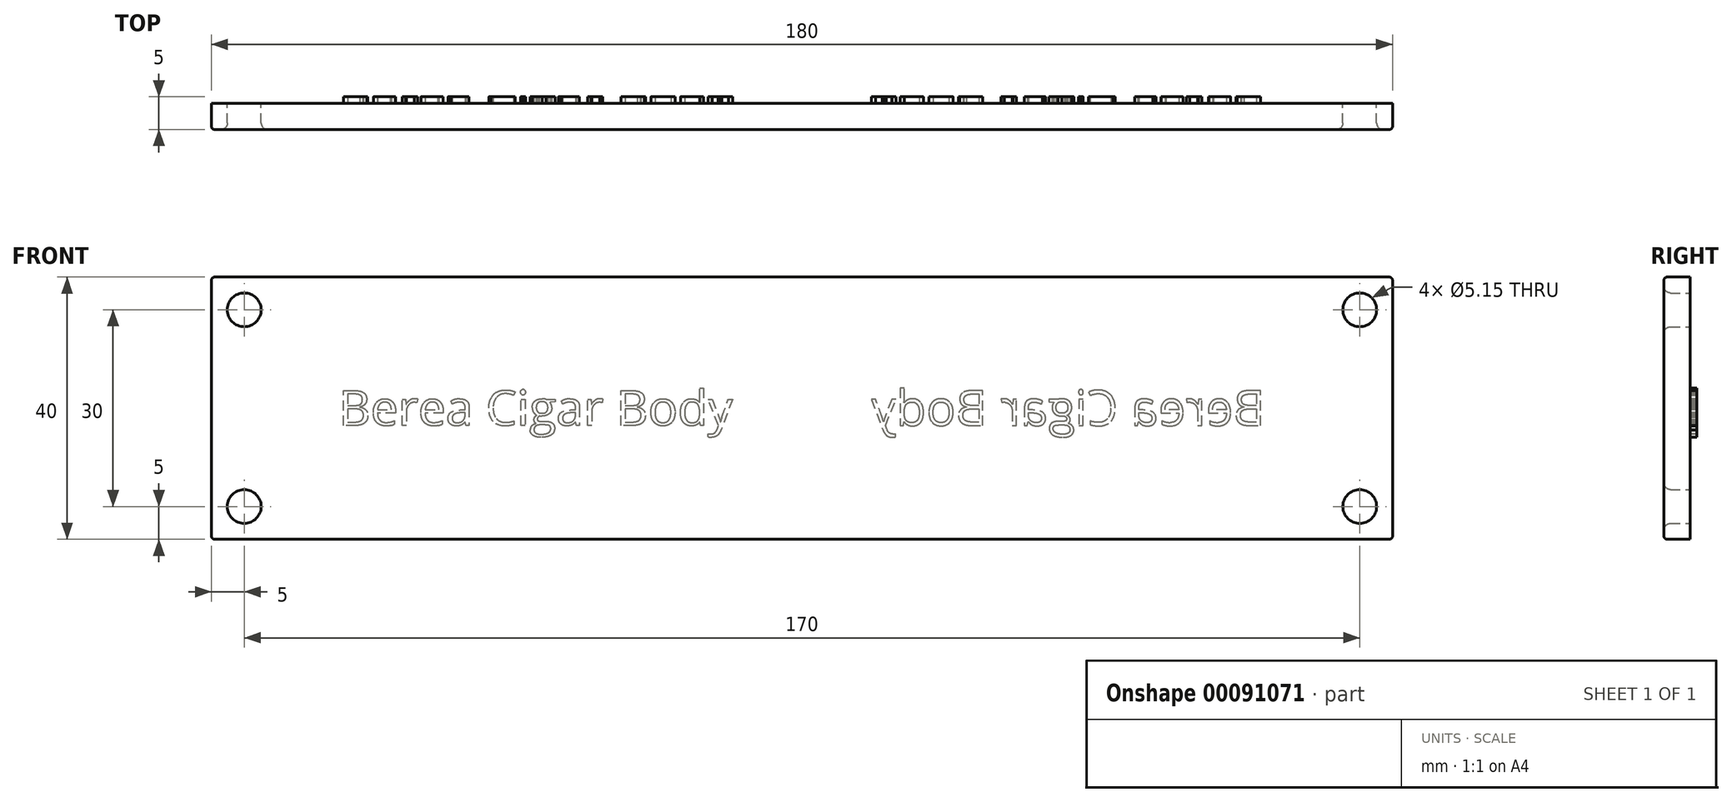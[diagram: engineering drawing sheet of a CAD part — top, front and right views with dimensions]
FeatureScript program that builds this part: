
annotation { "Feature Type Name" : "Feature", "Feature Type Description" : "" }
export const myFeature = defineFeature(function(context is Context, id is Id, definition is map)
    precondition{}
    {
        {
            var Q0;
            Q0=qCreatedBy(makeId("Front.planeOp"),FACE);
            var sketch = newSketch(context, id + "F0", { "sketchPlane" : qUnion([Q0])});
            skLineSegment(sketch, "E0.bottom", {"start": v(-90, -20) * mm, "end": v(90, -20) * mm});
            skLineSegment(sketch, "E0.top", {"start": v(-90, 20) * mm, "end": v(90, 20) * mm});
            skLineSegment(sketch, "E0.left", {"start": v(-90, -20) * mm, "end": v(-90, 20) * mm});
            skLineSegment(sketch, "E0.right", {"start": v(90, -20) * mm, "end": v(90, 20) * mm});
            skPoint(sketch, "E0.middle", {"position": v(0, 0) * mm});
            skCircle(sketch, "E1", {"center": v(-85, 15) * mm, "radius": 2.58 * mm});
            skPoint(sketch, "E2.start.orphan", {"position": v(-90, 0) * mm});
            skPoint(sketch, "E3.orphan", {"position": v(0, 20) * mm});
            skPoint(sketch, "E4.end.orphan", {"position": v(0, -20) * mm});
            skLineSegment(sketch, "E5", {"start": v(-90, 0) * mm, "end": v(0, 0) * mm, "construction": true});
            skLineSegment(sketch, "E6", {"start": v(0, 20) * mm, "end": v(0, -20) * mm, "construction": true});
            skCircle(sketch, "E7.MirrorC", {"center": v(-85, -15) * mm, "radius": 2.58 * mm});
            skCircle(sketch, "E8.MirrorC", {"center": v(85, 15) * mm, "radius": 2.58 * mm});
            skCircle(sketch, "E9.MirrorC", {"center": v(85, -15) * mm, "radius": 2.58 * mm});
            skSolve(sketch);
        }
        {
            var Q0;
            Q0=makeQuery(id+"F0.imprint","IMPRINT",FACE,{"disambiguationData":[TD([[makeQuery(id+"F0.imprint","IMPRINT",EDGE,{"derivedFrom":sQuery(id+"F0.wireOp",EDGE,"E0.bottom")}),1.0]])]});
            extrude(context, id + "F1", {"entities" : qUnion([Q0]), "depth" : 4 * mm});
        }
        {
            var Q0;
            Q0=makeQuery(id+"F1.opExtrude","CAP_EDGE",EDGE,{"disambiguationData":[OSD([sQuery(id+"F0.wireOp",EDGE,"E1")])],"isStart":false});
            var Q1;
            Q1=makeQuery(id+"F1.opExtrude","CAP_EDGE",EDGE,{"disambiguationData":[OSD([sQuery(id+"F0.wireOp",EDGE,"f5b72a5b-8583-449a-bdbf-9ac5a681e1fd0.MirrorC")])],"isStart":false});
            var Q2;
            Q2=makeQuery(id+"F1.opExtrude","CAP_EDGE",EDGE,{"disambiguationData":[OSD([sQuery(id+"F0.wireOp",EDGE,"2623e306-60f4-4522-aa65-1e3e8c2cf5b60.MirrorC")])],"isStart":false});
            var Q3;
            Q3=makeQuery(id+"F1.opExtrude","CAP_EDGE",EDGE,{"disambiguationData":[OSD([sQuery(id+"F0.wireOp",EDGE,"be81a34d-1d50-4ce7-a7a8-4484a1701fac0.MirrorC")])],"isStart":false});
            var Q4;
            Q4=makeQuery(id+"F1.opExtrude","CAP_EDGE",EDGE,{"disambiguationData":[OSD([sQuery(id+"F0.wireOp",EDGE,"E7.MirrorC")])],"isStart":false});
            var Q5;
            Q5=makeQuery(id+"F1.opExtrude","CAP_EDGE",EDGE,{"disambiguationData":[OSD([sQuery(id+"F0.wireOp",EDGE,"E8.MirrorC")])],"isStart":false});
            var Q6;
            Q6=makeQuery(id+"F1.opExtrude","CAP_EDGE",EDGE,{"disambiguationData":[OSD([sQuery(id+"F0.wireOp",EDGE,"E9.MirrorC")])],"isStart":false});
            fillet(context, id + "F2", {"entities" : qUnion([Q0, Q1, Q2, Q3, Q4, Q5, Q6]), "radius" : 1 * mm, "tangentPropagation" : true, "allowEdgeOverflow" : false});
        }
        {
            var Q0;
            Q0=makeQuery(id+"F1.opExtrude","CAP_EDGE",EDGE,{"disambiguationData":[OSD([sQuery(id+"F0.wireOp",EDGE,"E0.top")])],"isStart":false});
            var Q1;
            Q1=makeQuery(id+"F1.opExtrude","CAP_EDGE",EDGE,{"disambiguationData":[OSD([sQuery(id+"F0.wireOp",EDGE,"E0.left")])],"isStart":false});
            var Q2;
            Q2=makeQuery(id+"F1.opExtrude","CAP_EDGE",EDGE,{"disambiguationData":[OSD([sQuery(id+"F0.wireOp",EDGE,"E0.bottom")])],"isStart":false});
            var Q3;
            Q3=makeQuery(id+"F1.opExtrude","CAP_EDGE",EDGE,{"disambiguationData":[OSD([sQuery(id+"F0.wireOp",EDGE,"E0.right")])],"isStart":false});
            var Q4;
            Q4=makeQuery(id+"F1.opExtrude","SWEPT_EDGE",EDGE,{"disambiguationData":[OSD([sQuery(id+"F0.wireOp",EDGE,"E0.top"),sQuery(id+"F0.wireOp",EDGE,"E0.left")])]});
            var Q5;
            Q5=makeQuery(id+"F1.opExtrude","SWEPT_EDGE",EDGE,{"disambiguationData":[OSD([sQuery(id+"F0.wireOp",EDGE,"E0.bottom"),sQuery(id+"F0.wireOp",EDGE,"E0.left")])]});
            var Q6;
            Q6=makeQuery(id+"F1.opExtrude","SWEPT_EDGE",EDGE,{"disambiguationData":[OSD([sQuery(id+"F0.wireOp",EDGE,"E0.top"),sQuery(id+"F0.wireOp",EDGE,"E0.right")])]});
            var Q7;
            Q7=makeQuery(id+"F1.opExtrude","SWEPT_EDGE",EDGE,{"disambiguationData":[OSD([sQuery(id+"F0.wireOp",EDGE,"E0.bottom"),sQuery(id+"F0.wireOp",EDGE,"E0.right")])]});
            fillet(context, id + "F3", {"entities" : qUnion([Q0, Q1, Q2, Q3, Q4, Q5, Q6, Q7]), "radius" : .5 * mm, "tangentPropagation" : true, "allowEdgeOverflow" : false});
        }
        {
            var Q0;
            Q0=makeQuery(id+"F1.opExtrude","CAP_FACE",FACE,{"disambiguationData":[OSD([sQuery(id+"F0.wireOp",EDGE,"E0.bottom"),sQuery(id+"F0.wireOp",EDGE,"E0.top"),sQuery(id+"F0.wireOp",EDGE,"E0.left"),sQuery(id+"F0.wireOp",EDGE,"E0.right"),sQuery(id+"F0.wireOp",EDGE,"E1"),sQuery(id+"F0.wireOp",EDGE,"E7.MirrorC"),sQuery(id+"F0.wireOp",EDGE,"E8.MirrorC"),sQuery(id+"F0.wireOp",EDGE,"E9.MirrorC")])],"isStart":true});
            var sketch = newSketch(context, id + "F4", { "sketchPlane" : qUnion([Q0])});
            skText(sketch, "E10", { "text": "Berea Cigar Body", "fontName": "OpenSans-Regular.ttf"});
            skLineSegment(sketch, "E11", {"start": v(0, 20) * mm, "end": v(0, -20) * mm, "construction": true});
            const initialGuessF4  = {"E10": [-0.0706, -0.00264, 1, 0, 0.00539]};
            skSetInitialGuess(sketch, initialGuessF4);
            skSolve(sketch);
        }
        {
            var Q0;
            Q0=qSketchRegion(id+"F4",true);
            extrude(context, id + "F5", {"entities" : qUnion([Q0]), "operationType" : NewBodyOperationType.ADD, "depth" : 1 * mm});
        }
        {
            var Q0;
            Q0=makeQuery(id+"F1.opExtrude","SWEPT_BODY",BODY,{"disambiguationData":[OSD([sQuery(id+"F0.wireOp",EDGE,"E0.bottom"),sQuery(id+"F0.wireOp",EDGE,"E0.top"),sQuery(id+"F0.wireOp",EDGE,"E0.left"),sQuery(id+"F0.wireOp",EDGE,"E0.right"),sQuery(id+"F0.wireOp",EDGE,"E1"),sQuery(id+"F0.wireOp",EDGE,"E7.MirrorC"),sQuery(id+"F0.wireOp",EDGE,"E8.MirrorC"),sQuery(id+"F0.wireOp",EDGE,"E9.MirrorC")])]});
            var Q1;
            Q1=makeQuery(id+"F5.opExtrude","SWEPT_FACE",FACE,{"disambiguationData":[OSD([sQuery(id+"F4.wireOp",EDGE,"E10.sketch_text.stroke-94")])]});
            var Q2;
            Q2=makeQuery(id+"F5.opExtrude","SWEPT_FACE",FACE,{"disambiguationData":[OSD([sQuery(id+"F4.wireOp",EDGE,"E10.sketch_text.stroke-169")])]});
            var Q3;
            Q3=makeQuery(id+"F5.opExtrude","SWEPT_FACE",FACE,{"disambiguationData":[OSD([sQuery(id+"F4.wireOp",EDGE,"E10.sketch_text.stroke-185")])]});
            var Q4;
            Q4=makeQuery(id+"F5.opExtrude","SWEPT_FACE",FACE,{"disambiguationData":[OSD([sQuery(id+"F4.wireOp",EDGE,"E10.sketch_text.stroke-125")])]});
            var Q5;
            Q5=makeQuery(id+"F5.opExtrude","SWEPT_FACE",FACE,{"disambiguationData":[OSD([sQuery(id+"F4.wireOp",EDGE,"E10.sketch_text.stroke-155")])]});
            var Q6;
            Q6=makeQuery(id+"F5.opExtrude","SWEPT_FACE",FACE,{"disambiguationData":[OSD([sQuery(id+"F4.wireOp",EDGE,"E10.sketch_text.stroke-65")])]});
            var Q7;
            Q7=makeQuery(id+"F5.opExtrude","SWEPT_FACE",FACE,{"disambiguationData":[OSD([sQuery(id+"F4.wireOp",EDGE,"E10.sketch_text.stroke-81")])]});
            var Q8;
            Q8=makeQuery(id+"F5.opExtrude","SWEPT_FACE",FACE,{"disambiguationData":[OSD([sQuery(id+"F4.wireOp",EDGE,"E10.sketch_text.stroke-67")])]});
            var Q9;
            Q9=makeQuery(id+"F5.opExtrude","SWEPT_FACE",FACE,{"disambiguationData":[OSD([sQuery(id+"F4.wireOp",EDGE,"E10.sketch_text.stroke-99")])]});
            var Q10;
            Q10=makeQuery(id+"F5.opExtrude","SWEPT_FACE",FACE,{"disambiguationData":[OSD([sQuery(id+"F4.wireOp",EDGE,"E10.sketch_text.stroke-127")])]});
            var Q11;
            Q11=makeQuery(id+"F5.opExtrude","SWEPT_FACE",FACE,{"disambiguationData":[OSD([sQuery(id+"F4.wireOp",EDGE,"E10.sketch_text.stroke-10")])]});
            var Q12;
            Q12=makeQuery(id+"F5.opExtrude","CAP_FACE",FACE,{"disambiguationData":[OSD([sQuery(id+"F4.wireOp",EDGE,"E10.sketch_text.stroke-9"),sQuery(id+"F4.wireOp",EDGE,"E10.sketch_text.stroke-10"),sQuery(id+"F4.wireOp",EDGE,"E10.sketch_text.stroke-11"),sQuery(id+"F4.wireOp",EDGE,"E10.sketch_text.stroke-12")])],"isStart":false});
            var Q13;
            Q13=makeQuery(id+"F5.opExtrude","SWEPT_FACE",FACE,{"disambiguationData":[OSD([sQuery(id+"F4.wireOp",EDGE,"E10.sketch_text.stroke-154")])]});
            var Q14;
            Q14=makeQuery(id+"F5.opExtrude","SWEPT_FACE",FACE,{"disambiguationData":[OSD([sQuery(id+"F4.wireOp",EDGE,"E10.sketch_text.stroke-1")])]});
            var Q15;
            Q15=makeQuery(id+"F5.opExtrude","CAP_FACE",FACE,{"disambiguationData":[OSD([sQuery(id+"F4.wireOp",EDGE,"E10.sketch_text.stroke-124"),sQuery(id+"F4.wireOp",EDGE,"E10.sketch_text.stroke-125"),sQuery(id+"F4.wireOp",EDGE,"E10.sketch_text.stroke-126"),sQuery(id+"F4.wireOp",EDGE,"E10.sketch_text.stroke-127"),sQuery(id+"F4.wireOp",EDGE,"E10.sketch_text.stroke-128"),sQuery(id+"F4.wireOp",EDGE,"E10.sketch_text.stroke-129"),sQuery(id+"F4.wireOp",EDGE,"E10.sketch_text.stroke-130"),sQuery(id+"F4.wireOp",EDGE,"E10.sketch_text.stroke-131"),sQuery(id+"F4.wireOp",EDGE,"E10.sketch_text.stroke-132"),sQuery(id+"F4.wireOp",EDGE,"E10.sketch_text.stroke-133"),sQuery(id+"F4.wireOp",EDGE,"E10.sketch_text.stroke-134"),sQuery(id+"F4.wireOp",EDGE,"E10.sketch_text.stroke-135"),sQuery(id+"F4.wireOp",EDGE,"E10.sketch_text.stroke-136"),sQuery(id+"F4.wireOp",EDGE,"E10.sketch_text.stroke-137"),sQuery(id+"F4.wireOp",EDGE,"E10.sketch_text.stroke-138")])],"isStart":false});
            var Q16;
            Q16=makeQuery(id+"F5.opExtrude","CAP_FACE",FACE,{"disambiguationData":[OSD([sQuery(id+"F4.wireOp",EDGE,"E10.sketch_text.stroke-34"),sQuery(id+"F4.wireOp",EDGE,"E10.sketch_text.stroke-35"),sQuery(id+"F4.wireOp",EDGE,"E10.sketch_text.stroke-36"),sQuery(id+"F4.wireOp",EDGE,"E10.sketch_text.stroke-37"),sQuery(id+"F4.wireOp",EDGE,"E10.sketch_text.stroke-38"),sQuery(id+"F4.wireOp",EDGE,"E10.sketch_text.stroke-39"),sQuery(id+"F4.wireOp",EDGE,"E10.sketch_text.stroke-40"),sQuery(id+"F4.wireOp",EDGE,"E10.sketch_text.stroke-41"),sQuery(id+"F4.wireOp",EDGE,"E10.sketch_text.stroke-42"),sQuery(id+"F4.wireOp",EDGE,"E10.sketch_text.stroke-43"),sQuery(id+"F4.wireOp",EDGE,"E10.sketch_text.stroke-44"),sQuery(id+"F4.wireOp",EDGE,"E10.sketch_text.stroke-45"),sQuery(id+"F4.wireOp",EDGE,"E10.sketch_text.stroke-46"),sQuery(id+"F4.wireOp",EDGE,"E10.sketch_text.stroke-47"),sQuery(id+"F4.wireOp",EDGE,"E10.sketch_text.stroke-48"),sQuery(id+"F4.wireOp",EDGE,"E10.sketch_text.stroke-49"),sQuery(id+"F4.wireOp",EDGE,"E10.sketch_text.stroke-50"),sQuery(id+"F4.wireOp",EDGE,"E10.sketch_text.stroke-51"),sQuery(id+"F4.wireOp",EDGE,"E10.sketch_text.stroke-52"),sQuery(id+"F4.wireOp",EDGE,"E10.sketch_text.stroke-53"),sQuery(id+"F4.wireOp",EDGE,"E10.sketch_text.stroke-54"),sQuery(id+"F4.wireOp",EDGE,"E10.sketch_text.stroke-55"),sQuery(id+"F4.wireOp",EDGE,"E10.sketch_text.stroke-56"),sQuery(id+"F4.wireOp",EDGE,"E10.sketch_text.stroke-57"),sQuery(id+"F4.wireOp",EDGE,"E10.sketch_text.stroke-58"),sQuery(id+"F4.wireOp",EDGE,"E10.sketch_text.stroke-59"),sQuery(id+"F4.wireOp",EDGE,"E10.sketch_text.stroke-60")])],"isStart":false});
            var Q17;
            Q17=makeQuery(id+"F5.opExtrude","SWEPT_FACE",FACE,{"disambiguationData":[OSD([sQuery(id+"F4.wireOp",EDGE,"E10.sketch_text.stroke-50")])]});
            var Q18;
            Q18=makeQuery(id+"F5.opExtrude","SWEPT_FACE",FACE,{"disambiguationData":[OSD([sQuery(id+"F4.wireOp",EDGE,"E10.sketch_text.stroke-2")])]});
            var Q19;
            Q19=makeQuery(id+"F5.opExtrude","SWEPT_FACE",FACE,{"disambiguationData":[OSD([sQuery(id+"F4.wireOp",EDGE,"E10.sketch_text.stroke-3")])]});
            var Q20;
            Q20=makeQuery(id+"F5.opExtrude","SWEPT_FACE",FACE,{"disambiguationData":[OSD([sQuery(id+"F4.wireOp",EDGE,"E10.sketch_text.stroke-5")])]});
            var Q21;
            Q21=makeQuery(id+"F5.opExtrude","SWEPT_FACE",FACE,{"disambiguationData":[OSD([sQuery(id+"F4.wireOp",EDGE,"E10.sketch_text.stroke-8")])]});
            var Q22;
            Q22=makeQuery(id+"F5.opExtrude","SWEPT_FACE",FACE,{"disambiguationData":[OSD([sQuery(id+"F4.wireOp",EDGE,"E10.sketch_text.stroke-98")])]});
            var Q23;
            Q23=makeQuery(id+"F5.opExtrude","SWEPT_FACE",FACE,{"disambiguationData":[OSD([sQuery(id+"F4.wireOp",EDGE,"E10.sketch_text.stroke-66")])]});
            var Q24;
            Q24=makeQuery(id+"F5.opExtrude","SWEPT_FACE",FACE,{"disambiguationData":[OSD([sQuery(id+"F4.wireOp",EDGE,"E10.sketch_text.stroke-153")])]});
            var Q25;
            Q25=makeQuery(id+"F5.opExtrude","SWEPT_FACE",FACE,{"disambiguationData":[OSD([sQuery(id+"F4.wireOp",EDGE,"E10.sketch_text.stroke-126")])]});
            var Q26;
            Q26=makeQuery(id+"F5.opExtrude","SWEPT_FACE",FACE,{"disambiguationData":[OSD([sQuery(id+"F4.wireOp",EDGE,"E10.sketch_text.stroke-183")])]});
            var Q27;
            Q27=makeQuery(id+"F5.opExtrude","SWEPT_FACE",FACE,{"disambiguationData":[OSD([sQuery(id+"F4.wireOp",EDGE,"E10.sketch_text.stroke-109")])]});
            var Q28;
            Q28=makeQuery(id+"F5.opExtrude","SWEPT_FACE",FACE,{"disambiguationData":[OSD([sQuery(id+"F4.wireOp",EDGE,"E10.sketch_text.stroke-186")])]});
            var Q29;
            Q29=makeQuery(id+"F5.opExtrude","SWEPT_FACE",FACE,{"disambiguationData":[OSD([sQuery(id+"F4.wireOp",EDGE,"E10.sketch_text.stroke-79")])]});
            var Q30;
            Q30=makeQuery(id+"F5.opExtrude","SWEPT_FACE",FACE,{"disambiguationData":[OSD([sQuery(id+"F4.wireOp",EDGE,"E10.sketch_text.stroke-110")])]});
            var Q31;
            Q31=makeQuery(id+"F5.opExtrude","SWEPT_FACE",FACE,{"disambiguationData":[OSD([sQuery(id+"F4.wireOp",EDGE,"E10.sketch_text.stroke-38")])]});
            var Q32;
            Q32=makeQuery(id+"F5.opExtrude","SWEPT_FACE",FACE,{"disambiguationData":[OSD([sQuery(id+"F4.wireOp",EDGE,"E10.sketch_text.stroke-24")])]});
            var Q33;
            Q33=makeQuery(id+"F5.opExtrude","SWEPT_FACE",FACE,{"disambiguationData":[OSD([sQuery(id+"F4.wireOp",EDGE,"E10.sketch_text.stroke-12")])]});
            var Q34;
            Q34=makeQuery(id+"F5.opExtrude","SWEPT_FACE",FACE,{"disambiguationData":[OSD([sQuery(id+"F4.wireOp",EDGE,"E10.sketch_text.stroke-100")])]});
            var Q35;
            Q35=makeQuery(id+"F5.opExtrude","SWEPT_FACE",FACE,{"disambiguationData":[OSD([sQuery(id+"F4.wireOp",EDGE,"E10.sketch_text.stroke-158")])]});
            var Q36;
            Q36=makeQuery(id+"F5.opExtrude","SWEPT_FACE",FACE,{"disambiguationData":[OSD([sQuery(id+"F4.wireOp",EDGE,"E10.sketch_text.stroke-142")])]});
            var Q37;
            Q37=makeQuery(id+"F5.opExtrude","SWEPT_FACE",FACE,{"disambiguationData":[OSD([sQuery(id+"F4.wireOp",EDGE,"E10.sketch_text.stroke-54")])]});
            var Q38;
            Q38=makeQuery(id+"F5.opExtrude","SWEPT_FACE",FACE,{"disambiguationData":[OSD([sQuery(id+"F4.wireOp",EDGE,"E10.sketch_text.stroke-25")])]});
            var Q39;
            Q39=makeQuery(id+"F5.opExtrude","SWEPT_FACE",FACE,{"disambiguationData":[OSD([sQuery(id+"F4.wireOp",EDGE,"E10.sketch_text.stroke-101")])]});
            var Q40;
            Q40=makeQuery(id+"F5.opExtrude","SWEPT_FACE",FACE,{"disambiguationData":[OSD([sQuery(id+"F4.wireOp",EDGE,"E10.sketch_text.stroke-69")])]});
            var Q41;
            Q41=makeQuery(id+"F5.opExtrude","SWEPT_FACE",FACE,{"disambiguationData":[OSD([sQuery(id+"F4.wireOp",EDGE,"E10.sketch_text.stroke-159")])]});
            var Q42;
            Q42=makeQuery(id+"F5.opExtrude","SWEPT_FACE",FACE,{"disambiguationData":[OSD([sQuery(id+"F4.wireOp",EDGE,"E10.sketch_text.stroke-85")])]});
            var Q43;
            Q43=makeQuery(id+"F5.opExtrude","SWEPT_FACE",FACE,{"disambiguationData":[OSD([sQuery(id+"F4.wireOp",EDGE,"E10.sketch_text.stroke-173")])]});
            var Q44;
            Q44=makeQuery(id+"F5.opExtrude","SWEPT_FACE",FACE,{"disambiguationData":[OSD([sQuery(id+"F4.wireOp",EDGE,"E10.sketch_text.stroke-40")])]});
            var Q45;
            Q45=makeQuery(id+"F5.opExtrude","SWEPT_FACE",FACE,{"disambiguationData":[OSD([sQuery(id+"F4.wireOp",EDGE,"E10.sketch_text.stroke-102")])]});
            var Q46;
            Q46=makeQuery(id+"F5.opExtrude","SWEPT_FACE",FACE,{"disambiguationData":[OSD([sQuery(id+"F4.wireOp",EDGE,"E10.sketch_text.stroke-86")])]});
            var Q47;
            Q47=makeQuery(id+"F5.opExtrude","SWEPT_FACE",FACE,{"disambiguationData":[OSD([sQuery(id+"F4.wireOp",EDGE,"E10.sketch_text.stroke-130")])]});
            var Q48;
            Q48=makeQuery(id+"F5.opExtrude","SWEPT_FACE",FACE,{"disambiguationData":[OSD([sQuery(id+"F4.wireOp",EDGE,"E10.sketch_text.stroke-103")])]});
            var Q49;
            Q49=makeQuery(id+"F5.opExtrude","SWEPT_FACE",FACE,{"disambiguationData":[OSD([sQuery(id+"F4.wireOp",EDGE,"E10.sketch_text.stroke-87")])]});
            var Q50;
            Q50=makeQuery(id+"F5.opExtrude","SWEPT_FACE",FACE,{"disambiguationData":[OSD([sQuery(id+"F4.wireOp",EDGE,"E10.sketch_text.stroke-145")])]});
            var Q51;
            Q51=makeQuery(id+"F5.opExtrude","SWEPT_FACE",FACE,{"disambiguationData":[OSD([sQuery(id+"F4.wireOp",EDGE,"E10.sketch_text.stroke-131")])]});
            var Q52;
            Q52=makeQuery(id+"F5.opExtrude","SWEPT_FACE",FACE,{"disambiguationData":[OSD([sQuery(id+"F4.wireOp",EDGE,"E10.sketch_text.stroke-28")])]});
            var Q53;
            Q53=makeQuery(id+"F5.opExtrude","SWEPT_FACE",FACE,{"disambiguationData":[OSD([sQuery(id+"F4.wireOp",EDGE,"E10.sketch_text.stroke-14")])]});
            var Q54;
            Q54=makeQuery(id+"F5.opExtrude","SWEPT_FACE",FACE,{"disambiguationData":[OSD([sQuery(id+"F4.wireOp",EDGE,"E10.sketch_text.stroke-88")])]});
            var Q55;
            Q55=makeQuery(id+"F5.opExtrude","SWEPT_FACE",FACE,{"disambiguationData":[OSD([sQuery(id+"F4.wireOp",EDGE,"E10.sketch_text.stroke-162")])]});
            var Q56;
            Q56=makeQuery(id+"F5.opExtrude","SWEPT_FACE",FACE,{"disambiguationData":[OSD([sQuery(id+"F4.wireOp",EDGE,"E10.sketch_text.stroke-176")])]});
            var Q57;
            Q57=makeQuery(id+"F5.opExtrude","SWEPT_FACE",FACE,{"disambiguationData":[OSD([sQuery(id+"F4.wireOp",EDGE,"E10.sketch_text.stroke-73")])]});
            var Q58;
            Q58=makeQuery(id+"F5.opExtrude","SWEPT_FACE",FACE,{"disambiguationData":[OSD([sQuery(id+"F4.wireOp",EDGE,"E10.sketch_text.stroke-59")])]});
            var Q59;
            Q59=makeQuery(id+"F5.opExtrude","SWEPT_FACE",FACE,{"disambiguationData":[OSD([sQuery(id+"F4.wireOp",EDGE,"E10.sketch_text.stroke-133")])]});
            var Q60;
            Q60=makeQuery(id+"F5.opExtrude","SWEPT_FACE",FACE,{"disambiguationData":[OSD([sQuery(id+"F4.wireOp",EDGE,"E10.sketch_text.stroke-119")])]});
            var Q61;
            Q61=makeQuery(id+"F5.opExtrude","SWEPT_FACE",FACE,{"disambiguationData":[OSD([sQuery(id+"F4.wireOp",EDGE,"E10.sketch_text.stroke-74")])]});
            var Q62;
            Q62=makeQuery(id+"F5.opExtrude","SWEPT_FACE",FACE,{"disambiguationData":[OSD([sQuery(id+"F4.wireOp",EDGE,"E10.sketch_text.stroke-44")])]});
            var Q63;
            Q63=makeQuery(id+"F5.opExtrude","SWEPT_FACE",FACE,{"disambiguationData":[OSD([sQuery(id+"F4.wireOp",EDGE,"E10.sketch_text.stroke-120")])]});
            var Q64;
            Q64=makeQuery(id+"F5.opExtrude","SWEPT_FACE",FACE,{"disambiguationData":[OSD([sQuery(id+"F4.wireOp",EDGE,"E10.sketch_text.stroke-90")])]});
            var Q65;
            Q65=makeQuery(id+"F5.opExtrude","SWEPT_FACE",FACE,{"disambiguationData":[OSD([sQuery(id+"F4.wireOp",EDGE,"E10.sketch_text.stroke-178")])]});
            var Q66;
            Q66=makeQuery(id+"F5.opExtrude","SWEPT_FACE",FACE,{"disambiguationData":[OSD([sQuery(id+"F4.wireOp",EDGE,"E10.sketch_text.stroke-45")])]});
            var Q67;
            Q67=makeQuery(id+"F5.opExtrude","SWEPT_FACE",FACE,{"disambiguationData":[OSD([sQuery(id+"F4.wireOp",EDGE,"E10.sketch_text.stroke-31")])]});
            var Q68;
            Q68=makeQuery(id+"F5.opExtrude","SWEPT_FACE",FACE,{"disambiguationData":[OSD([sQuery(id+"F4.wireOp",EDGE,"E10.sketch_text.stroke-135")])]});
            var Q69;
            Q69=makeQuery(id+"F5.opExtrude","SWEPT_FACE",FACE,{"disambiguationData":[OSD([sQuery(id+"F4.wireOp",EDGE,"E10.sketch_text.stroke-179")])]});
            var Q70;
            Q70=makeQuery(id+"F5.opExtrude","SWEPT_FACE",FACE,{"disambiguationData":[OSD([sQuery(id+"F4.wireOp",EDGE,"E10.sketch_text.stroke-165")])]});
            var Q71;
            Q71=makeQuery(id+"F5.opExtrude","SWEPT_FACE",FACE,{"disambiguationData":[OSD([sQuery(id+"F4.wireOp",EDGE,"E10.sketch_text.stroke-149")])]});
            var Q72;
            Q72=makeQuery(id+"F5.opExtrude","SWEPT_FACE",FACE,{"disambiguationData":[OSD([sQuery(id+"F4.wireOp",EDGE,"E10.sketch_text.stroke-136")])]});
            var Q73;
            Q73=makeQuery(id+"F5.opExtrude","SWEPT_FACE",FACE,{"disambiguationData":[OSD([sQuery(id+"F4.wireOp",EDGE,"E10.sketch_text.stroke-122")])]});
            var Q74;
            Q74=makeQuery(id+"F5.opExtrude","SWEPT_FACE",FACE,{"disambiguationData":[OSD([sQuery(id+"F4.wireOp",EDGE,"E10.sketch_text.stroke-106")])]});
            var Q75;
            Q75=makeQuery(id+"F5.opExtrude","SWEPT_FACE",FACE,{"disambiguationData":[OSD([sQuery(id+"F4.wireOp",EDGE,"E10.sketch_text.stroke-180")])]});
            var Q76;
            Q76=makeQuery(id+"F5.opExtrude","SWEPT_FACE",FACE,{"disambiguationData":[OSD([sQuery(id+"F4.wireOp",EDGE,"E10.sketch_text.stroke-166")])]});
            var Q77;
            Q77=makeQuery(id+"F5.opExtrude","SWEPT_FACE",FACE,{"disambiguationData":[OSD([sQuery(id+"F4.wireOp",EDGE,"E10.sketch_text.stroke-150")])]});
            var Q78;
            Q78=makeQuery(id+"F5.opExtrude","SWEPT_FACE",FACE,{"disambiguationData":[OSD([sQuery(id+"F4.wireOp",EDGE,"E10.sketch_text.stroke-76")])]});
            var Q79;
            Q79=makeQuery(id+"F5.opExtrude","SWEPT_FACE",FACE,{"disambiguationData":[OSD([sQuery(id+"F4.wireOp",EDGE,"E10.sketch_text.stroke-32")])]});
            var Q80;
            Q80=makeQuery(id+"F5.opExtrude","SWEPT_FACE",FACE,{"disambiguationData":[OSD([sQuery(id+"F4.wireOp",EDGE,"E10.sketch_text.stroke-181")])]});
            var Q81;
            Q81=makeQuery(id+"F5.opExtrude","SWEPT_FACE",FACE,{"disambiguationData":[OSD([sQuery(id+"F4.wireOp",EDGE,"E10.sketch_text.stroke-47")])]});
            var Q82;
            Q82=makeQuery(id+"F5.opExtrude","SWEPT_FACE",FACE,{"disambiguationData":[OSD([sQuery(id+"F4.wireOp",EDGE,"E10.sketch_text.stroke-123")])]});
            var Q83;
            Q83=makeQuery(id+"F5.opExtrude","SWEPT_FACE",FACE,{"disambiguationData":[OSD([sQuery(id+"F4.wireOp",EDGE,"E10.sketch_text.stroke-107")])]});
            var Q84;
            Q84=makeQuery(id+"F5.opExtrude","SWEPT_FACE",FACE,{"disambiguationData":[OSD([sQuery(id+"F4.wireOp",EDGE,"E10.sketch_text.stroke-48")])]});
            var Q85;
            Q85=makeQuery(id+"F5.opExtrude","SWEPT_FACE",FACE,{"disambiguationData":[OSD([sQuery(id+"F4.wireOp",EDGE,"E10.sketch_text.stroke-124")])]});
            var Q86;
            Q86=makeQuery(id+"F5.opExtrude","SWEPT_FACE",FACE,{"disambiguationData":[OSD([sQuery(id+"F4.wireOp",EDGE,"E10.sketch_text.stroke-108")])]});
            var Q87;
            Q87=makeQuery(id+"F5.opExtrude","CAP_FACE",FACE,{"disambiguationData":[OSD([sQuery(id+"F4.wireOp",EDGE,"E10.sketch_text.stroke-139"),sQuery(id+"F4.wireOp",EDGE,"E10.sketch_text.stroke-140"),sQuery(id+"F4.wireOp",EDGE,"E10.sketch_text.stroke-141"),sQuery(id+"F4.wireOp",EDGE,"E10.sketch_text.stroke-142"),sQuery(id+"F4.wireOp",EDGE,"E10.sketch_text.stroke-143"),sQuery(id+"F4.wireOp",EDGE,"E10.sketch_text.stroke-144"),sQuery(id+"F4.wireOp",EDGE,"E10.sketch_text.stroke-145"),sQuery(id+"F4.wireOp",EDGE,"E10.sketch_text.stroke-146"),sQuery(id+"F4.wireOp",EDGE,"E10.sketch_text.stroke-147"),sQuery(id+"F4.wireOp",EDGE,"E10.sketch_text.stroke-148"),sQuery(id+"F4.wireOp",EDGE,"E10.sketch_text.stroke-149"),sQuery(id+"F4.wireOp",EDGE,"E10.sketch_text.stroke-150"),sQuery(id+"F4.wireOp",EDGE,"E10.sketch_text.stroke-151"),sQuery(id+"F4.wireOp",EDGE,"E10.sketch_text.stroke-152"),sQuery(id+"F4.wireOp",EDGE,"E10.sketch_text.stroke-153"),sQuery(id+"F4.wireOp",EDGE,"E10.sketch_text.stroke-154"),sQuery(id+"F4.wireOp",EDGE,"E10.sketch_text.stroke-155"),sQuery(id+"F4.wireOp",EDGE,"E10.sketch_text.stroke-156"),sQuery(id+"F4.wireOp",EDGE,"E10.sketch_text.stroke-157"),sQuery(id+"F4.wireOp",EDGE,"E10.sketch_text.stroke-158"),sQuery(id+"F4.wireOp",EDGE,"E10.sketch_text.stroke-159"),sQuery(id+"F4.wireOp",EDGE,"E10.sketch_text.stroke-160"),sQuery(id+"F4.wireOp",EDGE,"E10.sketch_text.stroke-161"),sQuery(id+"F4.wireOp",EDGE,"E10.sketch_text.stroke-162"),sQuery(id+"F4.wireOp",EDGE,"E10.sketch_text.stroke-163"),sQuery(id+"F4.wireOp",EDGE,"E10.sketch_text.stroke-164"),sQuery(id+"F4.wireOp",EDGE,"E10.sketch_text.stroke-165")])],"isStart":false});
            var Q88;
            Q88=makeQuery(id+"F5.opExtrude","CAP_FACE",FACE,{"disambiguationData":[OSD([sQuery(id+"F4.wireOp",EDGE,"E10.sketch_text.stroke-21"),sQuery(id+"F4.wireOp",EDGE,"E10.sketch_text.stroke-22"),sQuery(id+"F4.wireOp",EDGE,"E10.sketch_text.stroke-23"),sQuery(id+"F4.wireOp",EDGE,"E10.sketch_text.stroke-24"),sQuery(id+"F4.wireOp",EDGE,"E10.sketch_text.stroke-25"),sQuery(id+"F4.wireOp",EDGE,"E10.sketch_text.stroke-26"),sQuery(id+"F4.wireOp",EDGE,"E10.sketch_text.stroke-27"),sQuery(id+"F4.wireOp",EDGE,"E10.sketch_text.stroke-28"),sQuery(id+"F4.wireOp",EDGE,"E10.sketch_text.stroke-29"),sQuery(id+"F4.wireOp",EDGE,"E10.sketch_text.stroke-30"),sQuery(id+"F4.wireOp",EDGE,"E10.sketch_text.stroke-31"),sQuery(id+"F4.wireOp",EDGE,"E10.sketch_text.stroke-32"),sQuery(id+"F4.wireOp",EDGE,"E10.sketch_text.stroke-33")])],"isStart":false});
            var Q89;
            Q89=makeQuery(id+"F5.opExtrude","SWEPT_FACE",FACE,{"disambiguationData":[OSD([sQuery(id+"F4.wireOp",EDGE,"E10.sketch_text.stroke-113")])]});
            var Q90;
            Q90=makeQuery(id+"F5.opExtrude","SWEPT_FACE",FACE,{"disambiguationData":[OSD([sQuery(id+"F4.wireOp",EDGE,"E10.sketch_text.stroke-37")])]});
            var Q91;
            Q91=makeQuery(id+"F5.opExtrude","SWEPT_FACE",FACE,{"disambiguationData":[OSD([sQuery(id+"F4.wireOp",EDGE,"E10.sketch_text.stroke-187")])]});
            var Q92;
            Q92=makeQuery(id+"F5.opExtrude","SWEPT_FACE",FACE,{"disambiguationData":[OSD([sQuery(id+"F4.wireOp",EDGE,"E10.sketch_text.stroke-0")])]});
            var Q93;
            Q93=makeQuery(id+"F5.opExtrude","SWEPT_FACE",FACE,{"disambiguationData":[OSD([sQuery(id+"F4.wireOp",EDGE,"E10.sketch_text.stroke-4")])]});
            var Q94;
            Q94=makeQuery(id+"F5.opExtrude","SWEPT_FACE",FACE,{"disambiguationData":[OSD([sQuery(id+"F4.wireOp",EDGE,"E10.sketch_text.stroke-82")])]});
            var Q95;
            Q95=makeQuery(id+"F5.opExtrude","SWEPT_FACE",FACE,{"disambiguationData":[OSD([sQuery(id+"F4.wireOp",EDGE,"E10.sketch_text.stroke-52")])]});
            var Q96;
            Q96=makeQuery(id+"F5.opExtrude","SWEPT_FACE",FACE,{"disambiguationData":[OSD([sQuery(id+"F4.wireOp",EDGE,"E10.sketch_text.stroke-49")])]});
            var Q97;
            Q97=makeQuery(id+"F5.opExtrude","SWEPT_FACE",FACE,{"disambiguationData":[OSD([sQuery(id+"F4.wireOp",EDGE,"E10.sketch_text.stroke-63")])]});
            var Q98;
            Q98=makeQuery(id+"F5.opExtrude","SWEPT_FACE",FACE,{"disambiguationData":[OSD([sQuery(id+"F4.wireOp",EDGE,"E10.sketch_text.stroke-21")])]});
            var Q99;
            Q99=makeQuery(id+"F5.opExtrude","SWEPT_FACE",FACE,{"disambiguationData":[OSD([sQuery(id+"F4.wireOp",EDGE,"E10.sketch_text.stroke-128")])]});
            var Q100;
            Q100=makeQuery(id+"F5.opExtrude","SWEPT_FACE",FACE,{"disambiguationData":[OSD([sQuery(id+"F4.wireOp",EDGE,"E10.sketch_text.stroke-55")])]});
            var Q101;
            Q101=makeQuery(id+"F5.opExtrude","SWEPT_FACE",FACE,{"disambiguationData":[OSD([sQuery(id+"F4.wireOp",EDGE,"E10.sketch_text.stroke-26")])]});
            var Q102;
            Q102=makeQuery(id+"F5.opExtrude","SWEPT_FACE",FACE,{"disambiguationData":[OSD([sQuery(id+"F4.wireOp",EDGE,"E10.sketch_text.stroke-174")])]});
            var Q103;
            Q103=makeQuery(id+"F5.opExtrude","SWEPT_FACE",FACE,{"disambiguationData":[OSD([sQuery(id+"F4.wireOp",EDGE,"E10.sketch_text.stroke-104")])]});
            var Q104;
            Q104=makeQuery(id+"F5.opExtrude","SWEPT_FACE",FACE,{"disambiguationData":[OSD([sQuery(id+"F4.wireOp",EDGE,"E10.sketch_text.stroke-72")])]});
            var Q105;
            Q105=makeQuery(id+"F5.opExtrude","SWEPT_FACE",FACE,{"disambiguationData":[OSD([sQuery(id+"F4.wireOp",EDGE,"E10.sketch_text.stroke-132")])]});
            var Q106;
            Q106=makeQuery(id+"F5.opExtrude","SWEPT_FACE",FACE,{"disambiguationData":[OSD([sQuery(id+"F4.wireOp",EDGE,"E10.sketch_text.stroke-43")])]});
            var Q107;
            Q107=makeQuery(id+"F5.opExtrude","SWEPT_FACE",FACE,{"disambiguationData":[OSD([sQuery(id+"F4.wireOp",EDGE,"E10.sketch_text.stroke-15")])]});
            var Q108;
            Q108=makeQuery(id+"F5.opExtrude","SWEPT_FACE",FACE,{"disambiguationData":[OSD([sQuery(id+"F4.wireOp",EDGE,"E10.sketch_text.stroke-89")])]});
            var Q109;
            Q109=makeQuery(id+"F5.opExtrude","SWEPT_FACE",FACE,{"disambiguationData":[OSD([sQuery(id+"F4.wireOp",EDGE,"E10.sketch_text.stroke-163")])]});
            var Q110;
            Q110=makeQuery(id+"F5.opExtrude","SWEPT_FACE",FACE,{"disambiguationData":[OSD([sQuery(id+"F4.wireOp",EDGE,"E10.sketch_text.stroke-30")])]});
            var Q111;
            Q111=makeQuery(id+"F5.opExtrude","SWEPT_FACE",FACE,{"disambiguationData":[OSD([sQuery(id+"F4.wireOp",EDGE,"E10.sketch_text.stroke-134")])]});
            var Q112;
            Q112=makeQuery(id+"F5.opExtrude","SWEPT_FACE",FACE,{"disambiguationData":[OSD([sQuery(id+"F4.wireOp",EDGE,"E10.sketch_text.stroke-121")])]});
            var Q113;
            Q113=makeQuery(id+"F5.opExtrude","CAP_FACE",FACE,{"disambiguationData":[OSD([sQuery(id+"F4.wireOp",EDGE,"E10.sketch_text.stroke-105"),sQuery(id+"F4.wireOp",EDGE,"E10.sketch_text.stroke-106"),sQuery(id+"F4.wireOp",EDGE,"E10.sketch_text.stroke-107"),sQuery(id+"F4.wireOp",EDGE,"E10.sketch_text.stroke-108"),sQuery(id+"F4.wireOp",EDGE,"E10.sketch_text.stroke-109"),sQuery(id+"F4.wireOp",EDGE,"E10.sketch_text.stroke-110"),sQuery(id+"F4.wireOp",EDGE,"E10.sketch_text.stroke-111"),sQuery(id+"F4.wireOp",EDGE,"E10.sketch_text.stroke-112"),sQuery(id+"F4.wireOp",EDGE,"E10.sketch_text.stroke-113"),sQuery(id+"F4.wireOp",EDGE,"E10.sketch_text.stroke-114"),sQuery(id+"F4.wireOp",EDGE,"E10.sketch_text.stroke-115"),sQuery(id+"F4.wireOp",EDGE,"E10.sketch_text.stroke-116"),sQuery(id+"F4.wireOp",EDGE,"E10.sketch_text.stroke-117"),sQuery(id+"F4.wireOp",EDGE,"E10.sketch_text.stroke-118"),sQuery(id+"F4.wireOp",EDGE,"E10.sketch_text.stroke-119"),sQuery(id+"F4.wireOp",EDGE,"E10.sketch_text.stroke-120"),sQuery(id+"F4.wireOp",EDGE,"E10.sketch_text.stroke-121"),sQuery(id+"F4.wireOp",EDGE,"E10.sketch_text.stroke-122"),sQuery(id+"F4.wireOp",EDGE,"E10.sketch_text.stroke-123")])],"isStart":false});
            var Q114;
            Q114=makeQuery(id+"F5.opExtrude","SWEPT_FACE",FACE,{"disambiguationData":[OSD([sQuery(id+"F4.wireOp",EDGE,"E10.sketch_text.stroke-92")])]});
            var Q115;
            Q115=makeQuery(id+"F5.opExtrude","SWEPT_FACE",FACE,{"disambiguationData":[OSD([sQuery(id+"F4.wireOp",EDGE,"E10.sketch_text.stroke-46")])]});
            var Q116;
            Q116=makeQuery(id+"F5.opExtrude","CAP_FACE",FACE,{"disambiguationData":[OSD([sQuery(id+"F4.wireOp",EDGE,"E10.sketch_text.stroke-61"),sQuery(id+"F4.wireOp",EDGE,"E10.sketch_text.stroke-62"),sQuery(id+"F4.wireOp",EDGE,"E10.sketch_text.stroke-63"),sQuery(id+"F4.wireOp",EDGE,"E10.sketch_text.stroke-64"),sQuery(id+"F4.wireOp",EDGE,"E10.sketch_text.stroke-65"),sQuery(id+"F4.wireOp",EDGE,"E10.sketch_text.stroke-66"),sQuery(id+"F4.wireOp",EDGE,"E10.sketch_text.stroke-67"),sQuery(id+"F4.wireOp",EDGE,"E10.sketch_text.stroke-68"),sQuery(id+"F4.wireOp",EDGE,"E10.sketch_text.stroke-69"),sQuery(id+"F4.wireOp",EDGE,"E10.sketch_text.stroke-70"),sQuery(id+"F4.wireOp",EDGE,"E10.sketch_text.stroke-71"),sQuery(id+"F4.wireOp",EDGE,"E10.sketch_text.stroke-72"),sQuery(id+"F4.wireOp",EDGE,"E10.sketch_text.stroke-73"),sQuery(id+"F4.wireOp",EDGE,"E10.sketch_text.stroke-74"),sQuery(id+"F4.wireOp",EDGE,"E10.sketch_text.stroke-75"),sQuery(id+"F4.wireOp",EDGE,"E10.sketch_text.stroke-76"),sQuery(id+"F4.wireOp",EDGE,"E10.sketch_text.stroke-77"),sQuery(id+"F4.wireOp",EDGE,"E10.sketch_text.stroke-78"),sQuery(id+"F4.wireOp",EDGE,"E10.sketch_text.stroke-79"),sQuery(id+"F4.wireOp",EDGE,"E10.sketch_text.stroke-80"),sQuery(id+"F4.wireOp",EDGE,"E10.sketch_text.stroke-81"),sQuery(id+"F4.wireOp",EDGE,"E10.sketch_text.stroke-82"),sQuery(id+"F4.wireOp",EDGE,"E10.sketch_text.stroke-83"),sQuery(id+"F4.wireOp",EDGE,"E10.sketch_text.stroke-84"),sQuery(id+"F4.wireOp",EDGE,"E10.sketch_text.stroke-85"),sQuery(id+"F4.wireOp",EDGE,"E10.sketch_text.stroke-86"),sQuery(id+"F4.wireOp",EDGE,"E10.sketch_text.stroke-87"),sQuery(id+"F4.wireOp",EDGE,"E10.sketch_text.stroke-88"),sQuery(id+"F4.wireOp",EDGE,"E10.sketch_text.stroke-89"),sQuery(id+"F4.wireOp",EDGE,"E10.sketch_text.stroke-90"),sQuery(id+"F4.wireOp",EDGE,"E10.sketch_text.stroke-91"),sQuery(id+"F4.wireOp",EDGE,"E10.sketch_text.stroke-92"),sQuery(id+"F4.wireOp",EDGE,"E10.sketch_text.stroke-93"),sQuery(id+"F4.wireOp",EDGE,"E10.sketch_text.stroke-94"),sQuery(id+"F4.wireOp",EDGE,"E10.sketch_text.stroke-95"),sQuery(id+"F4.wireOp",EDGE,"E10.sketch_text.stroke-96"),sQuery(id+"F4.wireOp",EDGE,"E10.sketch_text.stroke-97"),sQuery(id+"F4.wireOp",EDGE,"E10.sketch_text.stroke-98"),sQuery(id+"F4.wireOp",EDGE,"E10.sketch_text.stroke-99"),sQuery(id+"F4.wireOp",EDGE,"E10.sketch_text.stroke-100"),sQuery(id+"F4.wireOp",EDGE,"E10.sketch_text.stroke-101"),sQuery(id+"F4.wireOp",EDGE,"E10.sketch_text.stroke-102"),sQuery(id+"F4.wireOp",EDGE,"E10.sketch_text.stroke-103"),sQuery(id+"F4.wireOp",EDGE,"E10.sketch_text.stroke-104")])],"isStart":false});
            var Q117;
            Q117=makeQuery(id+"F5.opExtrude","SWEPT_FACE",FACE,{"disambiguationData":[OSD([sQuery(id+"F4.wireOp",EDGE,"E10.sketch_text.stroke-33")])]});
            var Q118;
            Q118=makeQuery(id+"F5.opExtrude","SWEPT_FACE",FACE,{"disambiguationData":[OSD([sQuery(id+"F4.wireOp",EDGE,"E10.sketch_text.stroke-93")])]});
            var Q119;
            Q119=makeQuery(id+"F5.opExtrude","SWEPT_FACE",FACE,{"disambiguationData":[OSD([sQuery(id+"F4.wireOp",EDGE,"E10.sketch_text.stroke-34")])]});
            var Q120;
            Q120=makeQuery(id+"F5.opExtrude","SWEPT_FACE",FACE,{"disambiguationData":[OSD([sQuery(id+"F4.wireOp",EDGE,"E10.sketch_text.stroke-152")])]});
            var Q121;
            Q121=makeQuery(id+"F5.opExtrude","SWEPT_FACE",FACE,{"disambiguationData":[OSD([sQuery(id+"F4.wireOp",EDGE,"E10.sketch_text.stroke-51")])]});
            var Q122;
            Q122=makeQuery(id+"F5.opExtrude","SWEPT_FACE",FACE,{"disambiguationData":[OSD([sQuery(id+"F4.wireOp",EDGE,"E10.sketch_text.stroke-6")])]});
            var Q123;
            Q123=makeQuery(id+"F5.opExtrude","SWEPT_FACE",FACE,{"disambiguationData":[OSD([sQuery(id+"F4.wireOp",EDGE,"E10.sketch_text.stroke-7")])]});
            var Q124;
            Q124=makeQuery(id+"F5.opExtrude","SWEPT_FACE",FACE,{"disambiguationData":[OSD([sQuery(id+"F4.wireOp",EDGE,"E10.sketch_text.stroke-156")])]});
            var Q125;
            Q125=makeQuery(id+"F5.opExtrude","SWEPT_FACE",FACE,{"disambiguationData":[OSD([sQuery(id+"F4.wireOp",EDGE,"E10.sketch_text.stroke-112")])]});
            var Q126;
            Q126=makeQuery(id+"F5.boolean.opBoolean","SPLIT",FACE,{"disambiguationData":[TD([makeQuery(id+"F5.opExtrude","SWEPT_FACE",FACE,{"disambiguationData":[OSD([sQuery(id+"F4.wireOp",EDGE,"E10.sketch_text.stroke-182")])]})])],"derivedFrom":makeQuery(id+"F1.opExtrude","CAP_FACE",FACE,{"disambiguationData":[OSD([sQuery(id+"F0.wireOp",EDGE,"E0.bottom"),sQuery(id+"F0.wireOp",EDGE,"E0.top"),sQuery(id+"F0.wireOp",EDGE,"E0.left"),sQuery(id+"F0.wireOp",EDGE,"E0.right"),sQuery(id+"F0.wireOp",EDGE,"E1"),sQuery(id+"F0.wireOp",EDGE,"E7.MirrorC"),sQuery(id+"F0.wireOp",EDGE,"E8.MirrorC"),sQuery(id+"F0.wireOp",EDGE,"E9.MirrorC")])],"isStart":true})});
            var Q127;
            Q127=makeQuery(id+"F5.opExtrude","SWEPT_FACE",FACE,{"disambiguationData":[OSD([sQuery(id+"F4.wireOp",EDGE,"E10.sketch_text.stroke-96")])]});
            var Q128;
            Q128=makeQuery(id+"F5.opExtrude","SWEPT_FACE",FACE,{"disambiguationData":[OSD([sQuery(id+"F4.wireOp",EDGE,"E10.sketch_text.stroke-114")])]});
            var Q129;
            Q129=makeQuery(id+"F5.opExtrude","SWEPT_FACE",FACE,{"disambiguationData":[OSD([sQuery(id+"F4.wireOp",EDGE,"E10.sketch_text.stroke-39")])]});
            var Q130;
            Q130=makeQuery(id+"F5.opExtrude","SWEPT_FACE",FACE,{"disambiguationData":[OSD([sQuery(id+"F4.wireOp",EDGE,"E10.sketch_text.stroke-13")])]});
            var Q131;
            Q131=makeQuery(id+"F5.opExtrude","SWEPT_FACE",FACE,{"disambiguationData":[OSD([sQuery(id+"F4.wireOp",EDGE,"E10.sketch_text.stroke-115")])]});
            var Q132;
            Q132=makeQuery(id+"F5.opExtrude","SWEPT_FACE",FACE,{"disambiguationData":[OSD([sQuery(id+"F4.wireOp",EDGE,"E10.sketch_text.stroke-56")])]});
            var Q133;
            Q133=makeQuery(id+"F5.opExtrude","SWEPT_FACE",FACE,{"disambiguationData":[OSD([sQuery(id+"F4.wireOp",EDGE,"E10.sketch_text.stroke-144")])]});
            var Q134;
            Q134=makeQuery(id+"F5.opExtrude","SWEPT_FACE",FACE,{"disambiguationData":[OSD([sQuery(id+"F4.wireOp",EDGE,"E10.sketch_text.stroke-190")])]});
            var Q135;
            Q135=makeQuery(id+"F5.opExtrude","SWEPT_FACE",FACE,{"disambiguationData":[OSD([sQuery(id+"F4.wireOp",EDGE,"E10.sketch_text.stroke-116")])]});
            var Q136;
            Q136=makeQuery(id+"F5.opExtrude","SWEPT_FACE",FACE,{"disambiguationData":[OSD([sQuery(id+"F4.wireOp",EDGE,"E10.sketch_text.stroke-41")])]});
            var Q137;
            Q137=makeQuery(id+"F5.opExtrude","SWEPT_FACE",FACE,{"disambiguationData":[OSD([sQuery(id+"F4.wireOp",EDGE,"E10.sketch_text.stroke-161")])]});
            var Q138;
            Q138=makeQuery(id+"F5.opExtrude","SWEPT_FACE",FACE,{"disambiguationData":[OSD([sQuery(id+"F4.wireOp",EDGE,"E10.sketch_text.stroke-146")])]});
            var Q139;
            Q139=makeQuery(id+"F5.opExtrude","SWEPT_FACE",FACE,{"disambiguationData":[OSD([sQuery(id+"F4.wireOp",EDGE,"E10.sketch_text.stroke-58")])]});
            var Q140;
            Q140=makeQuery(id+"F5.opExtrude","SWEPT_FACE",FACE,{"disambiguationData":[OSD([sQuery(id+"F4.wireOp",EDGE,"E10.sketch_text.stroke-105")])]});
            var Q141;
            Q141=makeQuery(id+"F5.opExtrude","SWEPT_FACE",FACE,{"disambiguationData":[OSD([sQuery(id+"F4.wireOp",EDGE,"E10.sketch_text.stroke-177")])]});
            var Q142;
            Q142=makeQuery(id+"F5.opExtrude","SWEPT_FACE",FACE,{"disambiguationData":[OSD([sQuery(id+"F4.wireOp",EDGE,"E10.sketch_text.stroke-77")])]});
            var Q143;
            Q143=makeQuery(id+"F5.opExtrude","SWEPT_FACE",FACE,{"disambiguationData":[OSD([sQuery(id+"F4.wireOp",EDGE,"E10.sketch_text.stroke-138")])]});
            var Q144;
            Q144=makeQuery(id+"F5.opExtrude","SWEPT_FACE",FACE,{"disambiguationData":[OSD([sQuery(id+"F4.wireOp",EDGE,"E10.sketch_text.stroke-111")])]});
            var Q145;
            Q145=makeQuery(id+"F5.opExtrude","SWEPT_FACE",FACE,{"disambiguationData":[OSD([sQuery(id+"F4.wireOp",EDGE,"E10.sketch_text.stroke-53")])]});
            var Q146;
            Q146=makeQuery(id+"F5.opExtrude","SWEPT_FACE",FACE,{"disambiguationData":[OSD([sQuery(id+"F4.wireOp",EDGE,"E10.sketch_text.stroke-141")])]});
            var Q147;
            Q147=makeQuery(id+"F5.opExtrude","SWEPT_FACE",FACE,{"disambiguationData":[OSD([sQuery(id+"F4.wireOp",EDGE,"E10.sketch_text.stroke-157")])]});
            var Q148;
            Q148=makeQuery(id+"F5.opExtrude","SWEPT_FACE",FACE,{"disambiguationData":[OSD([sQuery(id+"F4.wireOp",EDGE,"E10.sketch_text.stroke-64")])]});
            var Q149;
            Q149=makeQuery(id+"F5.boolean.opBoolean","SPLIT",FACE,{"disambiguationData":[TD([makeQuery(id+"F5.opExtrude","SWEPT_FACE",FACE,{"disambiguationData":[OSD([sQuery(id+"F4.wireOp",EDGE,"E10.sketch_text.stroke-53")])]})])],"derivedFrom":makeQuery(id+"F1.opExtrude","CAP_FACE",FACE,{"disambiguationData":[OSD([sQuery(id+"F0.wireOp",EDGE,"E0.bottom"),sQuery(id+"F0.wireOp",EDGE,"E0.top"),sQuery(id+"F0.wireOp",EDGE,"E0.left"),sQuery(id+"F0.wireOp",EDGE,"E0.right"),sQuery(id+"F0.wireOp",EDGE,"E1"),sQuery(id+"F0.wireOp",EDGE,"E7.MirrorC"),sQuery(id+"F0.wireOp",EDGE,"E8.MirrorC"),sQuery(id+"F0.wireOp",EDGE,"E9.MirrorC")])],"isStart":true})});
            var Q150;
            Q150=makeQuery(id+"F5.opExtrude","SWEPT_FACE",FACE,{"disambiguationData":[OSD([sQuery(id+"F4.wireOp",EDGE,"E10.sketch_text.stroke-36")])]});
            var Q151;
            Q151=makeQuery(id+"F5.opExtrude","SWEPT_FACE",FACE,{"disambiguationData":[OSD([sQuery(id+"F4.wireOp",EDGE,"E10.sketch_text.stroke-22")])]});
            var Q152;
            Q152=makeQuery(id+"F5.boolean.opBoolean","SPLIT",FACE,{"disambiguationData":[TD([makeQuery(id+"F5.opExtrude","SWEPT_FACE",FACE,{"disambiguationData":[OSD([sQuery(id+"F4.wireOp",EDGE,"E10.sketch_text.stroke-119")])]})])],"derivedFrom":makeQuery(id+"F1.opExtrude","CAP_FACE",FACE,{"disambiguationData":[OSD([sQuery(id+"F0.wireOp",EDGE,"E0.bottom"),sQuery(id+"F0.wireOp",EDGE,"E0.top"),sQuery(id+"F0.wireOp",EDGE,"E0.left"),sQuery(id+"F0.wireOp",EDGE,"E0.right"),sQuery(id+"F0.wireOp",EDGE,"E1"),sQuery(id+"F0.wireOp",EDGE,"E7.MirrorC"),sQuery(id+"F0.wireOp",EDGE,"E8.MirrorC"),sQuery(id+"F0.wireOp",EDGE,"E9.MirrorC")])],"isStart":true})});
            var Q153;
            Q153=makeQuery(id+"F5.boolean.opBoolean","SPLIT",FACE,{"disambiguationData":[TD([makeQuery(id+"F5.opExtrude","SWEPT_FACE",FACE,{"disambiguationData":[OSD([sQuery(id+"F4.wireOp",EDGE,"E10.sketch_text.stroke-158")])]})])],"derivedFrom":makeQuery(id+"F1.opExtrude","CAP_FACE",FACE,{"disambiguationData":[OSD([sQuery(id+"F0.wireOp",EDGE,"E0.bottom"),sQuery(id+"F0.wireOp",EDGE,"E0.top"),sQuery(id+"F0.wireOp",EDGE,"E0.left"),sQuery(id+"F0.wireOp",EDGE,"E0.right"),sQuery(id+"F0.wireOp",EDGE,"E1"),sQuery(id+"F0.wireOp",EDGE,"E7.MirrorC"),sQuery(id+"F0.wireOp",EDGE,"E8.MirrorC"),sQuery(id+"F0.wireOp",EDGE,"E9.MirrorC")])],"isStart":true})});
            var Q154;
            Q154=makeQuery(id+"F5.opExtrude","SWEPT_FACE",FACE,{"disambiguationData":[OSD([sQuery(id+"F4.wireOp",EDGE,"E10.sketch_text.stroke-9")])]});
            var Q155;
            Q155=makeQuery(id+"F5.opExtrude","SWEPT_FACE",FACE,{"disambiguationData":[OSD([sQuery(id+"F4.wireOp",EDGE,"E10.sketch_text.stroke-167")])]});
            var Q156;
            Q156=makeQuery(id+"F5.opExtrude","SWEPT_FACE",FACE,{"disambiguationData":[OSD([sQuery(id+"F4.wireOp",EDGE,"E10.sketch_text.stroke-95")])]});
            var Q157;
            Q157=makeQuery(id+"F5.opExtrude","SWEPT_FACE",FACE,{"disambiguationData":[OSD([sQuery(id+"F4.wireOp",EDGE,"E10.sketch_text.stroke-184")])]});
            var Q158;
            Q158=makeQuery(id+"F5.opExtrude","SWEPT_FACE",FACE,{"disambiguationData":[OSD([sQuery(id+"F4.wireOp",EDGE,"E10.sketch_text.stroke-84")])]});
            var Q159;
            Q159=makeQuery(id+"F5.opExtrude","SWEPT_FACE",FACE,{"disambiguationData":[OSD([sQuery(id+"F4.wireOp",EDGE,"E10.sketch_text.stroke-68")])]});
            var Q160;
            Q160=makeQuery(id+"F5.opExtrude","SWEPT_FACE",FACE,{"disambiguationData":[OSD([sQuery(id+"F4.wireOp",EDGE,"E10.sketch_text.stroke-143")])]});
            var Q161;
            Q161=makeQuery(id+"F5.opExtrude","SWEPT_FACE",FACE,{"disambiguationData":[OSD([sQuery(id+"F4.wireOp",EDGE,"E10.sketch_text.stroke-189")])]});
            var Q162;
            Q162=makeQuery(id+"F5.opExtrude","CAP_FACE",FACE,{"disambiguationData":[OSD([sQuery(id+"F4.wireOp",EDGE,"E10.sketch_text.stroke-13"),sQuery(id+"F4.wireOp",EDGE,"E10.sketch_text.stroke-14"),sQuery(id+"F4.wireOp",EDGE,"E10.sketch_text.stroke-15"),sQuery(id+"F4.wireOp",EDGE,"E10.sketch_text.stroke-16"),sQuery(id+"F4.wireOp",EDGE,"E10.sketch_text.stroke-17"),sQuery(id+"F4.wireOp",EDGE,"E10.sketch_text.stroke-18"),sQuery(id+"F4.wireOp",EDGE,"E10.sketch_text.stroke-19"),sQuery(id+"F4.wireOp",EDGE,"E10.sketch_text.stroke-20")])],"isStart":false});
            var Q163;
            Q163=makeQuery(id+"F5.opExtrude","SWEPT_FACE",FACE,{"disambiguationData":[OSD([sQuery(id+"F4.wireOp",EDGE,"E10.sketch_text.stroke-57")])]});
            var Q164;
            Q164=makeQuery(id+"F5.opExtrude","SWEPT_FACE",FACE,{"disambiguationData":[OSD([sQuery(id+"F4.wireOp",EDGE,"E10.sketch_text.stroke-29")])]});
            var Q165;
            Q165=makeQuery(id+"F5.opExtrude","SWEPT_FACE",FACE,{"disambiguationData":[OSD([sQuery(id+"F4.wireOp",EDGE,"E10.sketch_text.stroke-60")])]});
            var Q166;
            Q166=makeQuery(id+"F5.opExtrude","SWEPT_FACE",FACE,{"disambiguationData":[OSD([sQuery(id+"F4.wireOp",EDGE,"E10.sketch_text.stroke-148")])]});
            var Q167;
            Q167=makeQuery(id+"F5.opExtrude","SWEPT_FACE",FACE,{"disambiguationData":[OSD([sQuery(id+"F4.wireOp",EDGE,"E10.sketch_text.stroke-75")])]});
            var Q168;
            Q168=makeQuery(id+"F5.opExtrude","SWEPT_FACE",FACE,{"disambiguationData":[OSD([sQuery(id+"F4.wireOp",EDGE,"E10.sketch_text.stroke-91")])]});
            var Q169;
            Q169=makeQuery(id+"F5.opExtrude","SWEPT_FACE",FACE,{"disambiguationData":[OSD([sQuery(id+"F4.wireOp",EDGE,"E10.sketch_text.stroke-78")])]});
            var Q170;
            Q170=makeQuery(id+"F5.opExtrude","SWEPT_FACE",FACE,{"disambiguationData":[OSD([sQuery(id+"F4.wireOp",EDGE,"E10.sketch_text.stroke-62")])]});
            var Q171;
            Q171=makeQuery(id+"F5.opExtrude","SWEPT_FACE",FACE,{"disambiguationData":[OSD([sQuery(id+"F4.wireOp",EDGE,"E10.sketch_text.stroke-182")])]});
            var Q172;
            Q172=makeQuery(id+"F5.opExtrude","SWEPT_FACE",FACE,{"disambiguationData":[OSD([sQuery(id+"F4.wireOp",EDGE,"E10.sketch_text.stroke-11")])]});
            var Q173;
            Q173=makeQuery(id+"F5.opExtrude","SWEPT_FACE",FACE,{"disambiguationData":[OSD([sQuery(id+"F4.wireOp",EDGE,"E10.sketch_text.stroke-97")])]});
            var Q174;
            Q174=makeQuery(id+"F5.opExtrude","SWEPT_FACE",FACE,{"disambiguationData":[OSD([sQuery(id+"F4.wireOp",EDGE,"E10.sketch_text.stroke-23")])]});
            var Q175;
            Q175=makeQuery(id+"F5.opExtrude","SWEPT_FACE",FACE,{"disambiguationData":[OSD([sQuery(id+"F4.wireOp",EDGE,"E10.sketch_text.stroke-80")])]});
            var Q176;
            Q176=makeQuery(id+"F5.boolean.opBoolean","SPLIT",FACE,{"disambiguationData":[TD([makeQuery(id+"F5.opExtrude","SWEPT_FACE",FACE,{"disambiguationData":[OSD([sQuery(id+"F4.wireOp",EDGE,"E10.sketch_text.stroke-99")])]})])],"derivedFrom":makeQuery(id+"F1.opExtrude","CAP_FACE",FACE,{"disambiguationData":[OSD([sQuery(id+"F0.wireOp",EDGE,"E0.bottom"),sQuery(id+"F0.wireOp",EDGE,"E0.top"),sQuery(id+"F0.wireOp",EDGE,"E0.left"),sQuery(id+"F0.wireOp",EDGE,"E0.right"),sQuery(id+"F0.wireOp",EDGE,"E1"),sQuery(id+"F0.wireOp",EDGE,"E7.MirrorC"),sQuery(id+"F0.wireOp",EDGE,"E8.MirrorC"),sQuery(id+"F0.wireOp",EDGE,"E9.MirrorC")])],"isStart":true})});
            var Q177;
            Q177=makeQuery(id+"F5.opExtrude","SWEPT_FACE",FACE,{"disambiguationData":[OSD([sQuery(id+"F4.wireOp",EDGE,"E10.sketch_text.stroke-168")])]});
            var Q178;
            Q178=makeQuery(id+"F5.opExtrude","SWEPT_FACE",FACE,{"disambiguationData":[OSD([sQuery(id+"F4.wireOp",EDGE,"E10.sketch_text.stroke-188")])]});
            var Q179;
            Q179=makeQuery(id+"F5.opExtrude","SWEPT_FACE",FACE,{"disambiguationData":[OSD([sQuery(id+"F4.wireOp",EDGE,"E10.sketch_text.stroke-129")])]});
            var Q180;
            Q180=makeQuery(id+"F5.opExtrude","SWEPT_FACE",FACE,{"disambiguationData":[OSD([sQuery(id+"F4.wireOp",EDGE,"E10.sketch_text.stroke-27")])]});
            var Q181;
            Q181=makeQuery(id+"F5.opExtrude","SWEPT_FACE",FACE,{"disambiguationData":[OSD([sQuery(id+"F4.wireOp",EDGE,"E10.sketch_text.stroke-175")])]});
            var Q182;
            Q182=makeQuery(id+"F5.opExtrude","SWEPT_FACE",FACE,{"disambiguationData":[OSD([sQuery(id+"F4.wireOp",EDGE,"E10.sketch_text.stroke-42")])]});
            var Q183;
            Q183=makeQuery(id+"F5.opExtrude","SWEPT_FACE",FACE,{"disambiguationData":[OSD([sQuery(id+"F4.wireOp",EDGE,"E10.sketch_text.stroke-118")])]});
            var Q184;
            Q184=makeQuery(id+"F5.opExtrude","SWEPT_FACE",FACE,{"disambiguationData":[OSD([sQuery(id+"F4.wireOp",EDGE,"E10.sketch_text.stroke-151")])]});
            var Q185;
            Q185=makeQuery(id+"F5.opExtrude","SWEPT_FACE",FACE,{"disambiguationData":[OSD([sQuery(id+"F4.wireOp",EDGE,"E10.sketch_text.stroke-137")])]});
            var Q186;
            Q186=makeQuery(id+"F5.opExtrude","SWEPT_FACE",FACE,{"disambiguationData":[OSD([sQuery(id+"F4.wireOp",EDGE,"E10.sketch_text.stroke-83")])]});
            var Q187;
            Q187=makeQuery(id+"F5.boolean.opBoolean","SPLIT",FACE,{"disambiguationData":[TD([makeQuery(id+"F5.opExtrude","SWEPT_FACE",FACE,{"disambiguationData":[OSD([sQuery(id+"F4.wireOp",EDGE,"E10.sketch_text.stroke-90")])]})])],"derivedFrom":makeQuery(id+"F1.opExtrude","CAP_FACE",FACE,{"disambiguationData":[OSD([sQuery(id+"F0.wireOp",EDGE,"E0.bottom"),sQuery(id+"F0.wireOp",EDGE,"E0.top"),sQuery(id+"F0.wireOp",EDGE,"E0.left"),sQuery(id+"F0.wireOp",EDGE,"E0.right"),sQuery(id+"F0.wireOp",EDGE,"E1"),sQuery(id+"F0.wireOp",EDGE,"E7.MirrorC"),sQuery(id+"F0.wireOp",EDGE,"E8.MirrorC"),sQuery(id+"F0.wireOp",EDGE,"E9.MirrorC")])],"isStart":true})});
            var Q188;
            Q188=makeQuery(id+"F5.opExtrude","SWEPT_FACE",FACE,{"disambiguationData":[OSD([sQuery(id+"F4.wireOp",EDGE,"E10.sketch_text.stroke-139")])]});
            var Q189;
            Q189=makeQuery(id+"F5.opExtrude","SWEPT_FACE",FACE,{"disambiguationData":[OSD([sQuery(id+"F4.wireOp",EDGE,"E10.sketch_text.stroke-70")])]});
            var Q190;
            Q190=makeQuery(id+"F5.opExtrude","SWEPT_FACE",FACE,{"disambiguationData":[OSD([sQuery(id+"F4.wireOp",EDGE,"E10.sketch_text.stroke-160")])]});
            var Q191;
            Q191=makeQuery(id+"F5.opExtrude","SWEPT_FACE",FACE,{"disambiguationData":[OSD([sQuery(id+"F4.wireOp",EDGE,"E10.sketch_text.stroke-71")])]});
            var Q192;
            Q192=makeQuery(id+"F5.opExtrude","SWEPT_FACE",FACE,{"disambiguationData":[OSD([sQuery(id+"F4.wireOp",EDGE,"E10.sketch_text.stroke-117")])]});
            var Q193;
            Q193=makeQuery(id+"F5.opExtrude","SWEPT_FACE",FACE,{"disambiguationData":[OSD([sQuery(id+"F4.wireOp",EDGE,"E10.sketch_text.stroke-147")])]});
            var Q194;
            Q194=makeQuery(id+"F5.opExtrude","SWEPT_FACE",FACE,{"disambiguationData":[OSD([sQuery(id+"F4.wireOp",EDGE,"E10.sketch_text.stroke-164")])]});
            var Q195;
            Q195=makeQuery(id+"F5.opExtrude","SWEPT_FACE",FACE,{"disambiguationData":[OSD([sQuery(id+"F4.wireOp",EDGE,"E10.sketch_text.stroke-61")])]});
            var Q196;
            Q196=makeQuery(id+"F5.opExtrude","SWEPT_FACE",FACE,{"disambiguationData":[OSD([sQuery(id+"F4.wireOp",EDGE,"E10.sketch_text.stroke-19")])]});
            var Q197;
            Q197=makeQuery(id+"F5.opExtrude","SWEPT_FACE",FACE,{"disambiguationData":[OSD([sQuery(id+"F4.wireOp",EDGE,"E10.sketch_text.stroke-35")])]});
            var Q198;
            Q198=makeQuery(id+"F5.opExtrude","SWEPT_FACE",FACE,{"disambiguationData":[OSD([sQuery(id+"F4.wireOp",EDGE,"E10.sketch_text.stroke-140")])]});
            var Q199;
            Q199=makeQuery(id+"F5.opExtrude","SWEPT_FACE",FACE,{"disambiguationData":[OSD([sQuery(id+"F4.wireOp",EDGE,"E10.sketch_text.stroke-20")])]});
            var Q200;
            Q200=makeQuery(id+"F5.opExtrude","SWEPT_FACE",FACE,{"disambiguationData":[OSD([sQuery(id+"F4.wireOp",EDGE,"E10.sketch_text.stroke-16")])]});
            var Q201;
            Q201=makeQuery(id+"F5.opExtrude","SWEPT_FACE",FACE,{"disambiguationData":[OSD([sQuery(id+"F4.wireOp",EDGE,"E10.sketch_text.stroke-18")])]});
            var Q202;
            Q202=makeQuery(id+"F5.opExtrude","SWEPT_FACE",FACE,{"disambiguationData":[OSD([sQuery(id+"F4.wireOp",EDGE,"E10.sketch_text.stroke-17")])]});
            var Q203;
            Q203=qCreatedBy(makeId("Right.planeOp"),FACE);
            mirror(context, id + "F6", {"operationType" : NewBodyOperationType.ADD, "entities" : qUnion([Q0]), "faces" : qUnion([Q1, Q2, Q3, Q4, Q5, Q6, Q7, Q8, Q9, Q10, Q11, Q12, Q13, Q14, Q15, Q16, Q17, Q18, Q19, Q20, Q21, Q22, Q23, Q24, Q25, Q26, Q27, Q28, Q29, Q30, Q31, Q32, Q33, Q34, Q35, Q36, Q37, Q38, Q39, Q40, Q41, Q42, Q43, Q44, Q45, Q46, Q47, Q48, Q49, Q50, Q51, Q52, Q53, Q54, Q55, Q56, Q57, Q58, Q59, Q60, Q61, Q62, Q63, Q64, Q65, Q66, Q67, Q68, Q69, Q70, Q71, Q72, Q73, Q74, Q75, Q76, Q77, Q78, Q79, Q80, Q81, Q82, Q83, Q84, Q85, Q86, Q87, Q88, Q89, Q90, Q91, Q92, Q93, Q94, Q95, Q96, Q97, Q98, Q99, Q100, Q101, Q102, Q103, Q104, Q105, Q106, Q107, Q108, Q109, Q110, Q111, Q112, Q113, Q114, Q115, Q116, Q117, Q118, Q119, Q120, Q121, Q122, Q123, Q124, Q125, Q126, Q127, Q128, Q129, Q130, Q131, Q132, Q133, Q134, Q135, Q136, Q137, Q138, Q139, Q140, Q141, Q142, Q143, Q144, Q145, Q146, Q147, Q148, Q149, Q150, Q151, Q152, Q153, Q154, Q155, Q156, Q157, Q158, Q159, Q160, Q161, Q162, Q163, Q164, Q165, Q166, Q167, Q168, Q169, Q170, Q171, Q172, Q173, Q174, Q175, Q176, Q177, Q178, Q179, Q180, Q181, Q182, Q183, Q184, Q185, Q186, Q187, Q188, Q189, Q190, Q191, Q192, Q193, Q194, Q195, Q196, Q197, Q198, Q199, Q200, Q201, Q202]), "mirrorPlane" : qUnion([Q203])});
        }
    });
